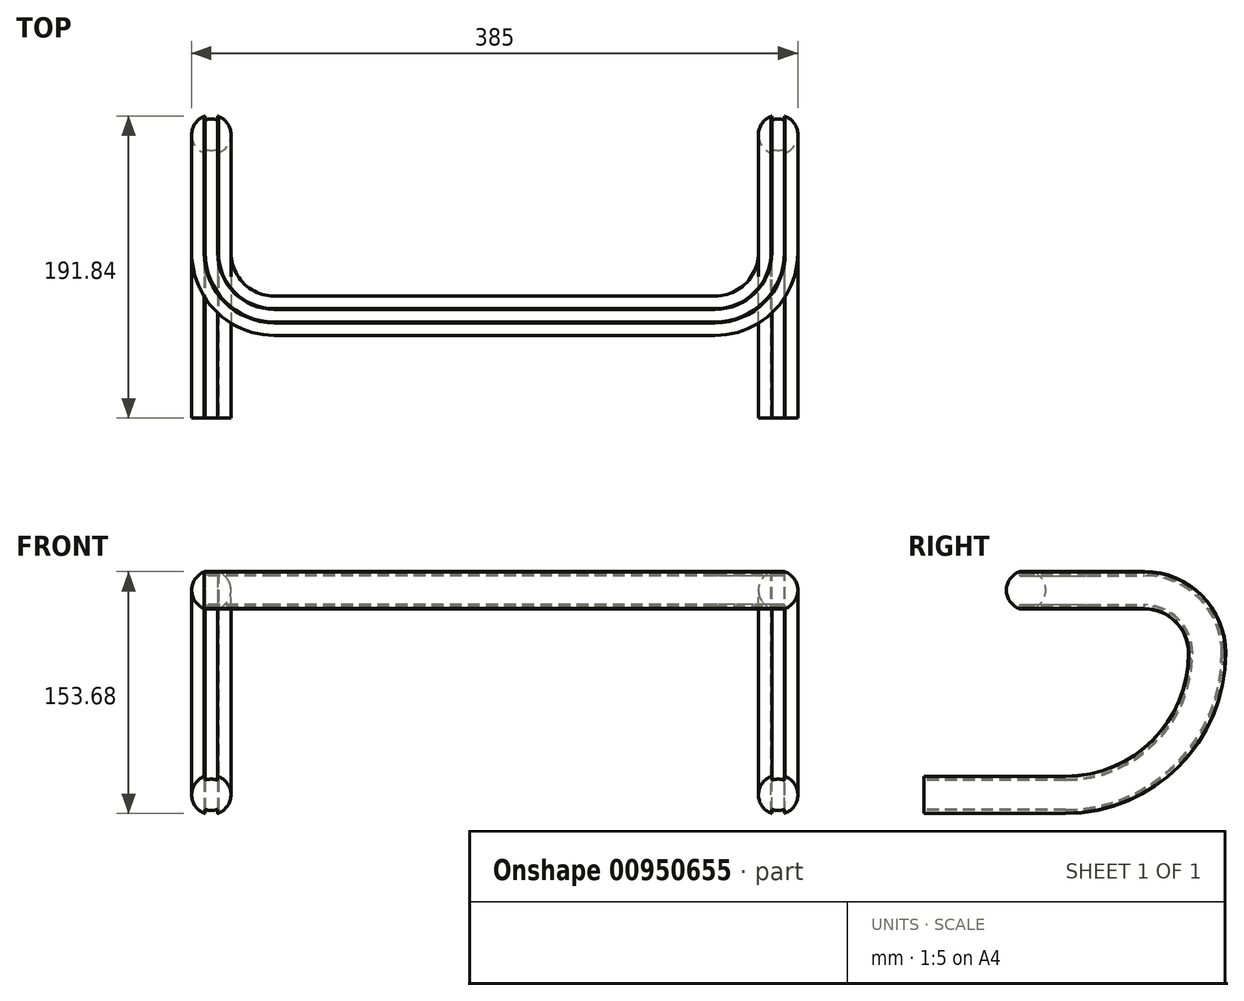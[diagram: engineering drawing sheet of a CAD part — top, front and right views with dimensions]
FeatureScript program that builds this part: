
annotation { "Feature Type Name" : "Feature", "Feature Type Description" : "" }
export const myFeature = defineFeature(function(context is Context, id is Id, definition is map)
    precondition{}
    {
        {
            var Q0;
            Q0=qCreatedBy(makeId("Top.planeOp"),FACE);
            var sketch = newSketch(context, id + "F0", { "sketchPlane" : qUnion([Q0])});
            skLineSegment(sketch, "E0", {"start": v(-140, 0) * mm, "end": v(140, 0) * mm});
            skArc(sketch, "E1", {"start": v(-180, 40) * mm, "mid": v(-168.28, 11.72) * mm, "end": v(-140, 0) * mm});
            skArc(sketch, "E2", {"start": v(140, 0) * mm, "mid": v(168.28, 11.72) * mm, "end": v(180, 40) * mm});
            skSolve(sketch);
        }
        {
            var Q0;
            Q0=qCreatedBy(makeId("Right.planeOp"),FACE);
            var Q1;
            Q1=sQuery(id+"F0.wireOp",VERTEX,"E2.end");
            cPlane(context, id + "F1", {"entities" : qUnion([Q0, Q1]), "cplaneType" : CPlaneType.PLANE_POINT, "offset" : 25 * mm, "width" : 150 * mm, "height" : 150 * mm});
        }
        {
            var Q0;
            Q0=qCreatedBy(id+"F1.planeOp",FACE);
            var sketch = newSketch(context, id + "F2", { "sketchPlane" : qUnion([Q0])});
            skPoint(sketch, "E3.0", {"position": v(40, 0) * mm});
            skLineSegment(sketch, "E4", {"start": v(40, 0) * mm, "end": v(75, 0) * mm});
            skArc(sketch, "E5", {"start": v(115, -40) * mm, "mid": v(103.28, -11.72) * mm, "end": v(75, 0) * mm});
            skArc(sketch, "E6", {"start": v(25, -130) * mm, "mid": v(88.64, -103.64) * mm, "end": v(115, -40) * mm});
            skLineSegment(sketch, "E7", {"start": v(25, -130) * mm, "end": v(-65, -130) * mm});
            skSolve(sketch);
        }
        {
            var Q0;
            Q0=sQuery(id+"F0.wireOp",VERTEX,"E1.start");
            var Q1;
            Q1=qCreatedBy(id+"F1.planeOp",FACE);
            cPlane(context, id + "F3", {"entities" : qUnion([Q0, Q1]), "cplaneType" : CPlaneType.PLANE_POINT, "offset" : 25 * mm, "width" : 150 * mm, "height" : 150 * mm});
        }
        {
            var Q0;
            Q0=qCreatedBy(id+"F3.planeOp",FACE);
            var sketch = newSketch(context, id + "F4", { "sketchPlane" : qUnion([Q0])});
            skLineSegment(sketch, "E8.0", {"start": v(40, 0) * mm, "end": v(75, 0) * mm});
            skArc(sketch, "E8.1", {"start": v(115, -40) * mm, "mid": v(103.28, -11.72) * mm, "end": v(75, 0) * mm});
            skArc(sketch, "E8.2", {"start": v(25, -130) * mm, "mid": v(88.64, -103.64) * mm, "end": v(115, -40) * mm});
            skLineSegment(sketch, "E8.3", {"start": v(25, -130) * mm, "end": v(-65, -130) * mm});
            skSolve(sketch);
        }
        {
            var Q0;
            Q0=qCreatedBy(makeId("Front.planeOp"),FACE);
            var Q1;
            Q1=sQuery(id+"F2.wireOp",VERTEX,"E7.end");
            cPlane(context, id + "F5", {"entities" : qUnion([Q0, Q1]), "cplaneType" : CPlaneType.PLANE_POINT, "offset" : 25 * mm, "width" : 150 * mm, "height" : 150 * mm});
        }
        {
            var Q0;
            Q0=qCreatedBy(id+"F5.planeOp",FACE);
            var sketch = newSketch(context, id + "F6", { "sketchPlane" : qUnion([Q0])});
            skPoint(sketch, "E9.0", {"position": v(180, -130) * mm});
            skArc(sketch, "E10", {"start": v(175.5, -141.66) * mm, "mid": v(175.75, -141.75) * mm, "end": v(176, -141.84) * mm, "construction": true});
            skArc(sketch, "E11", {"start": v(176, -139.17) * mm, "mid": v(180, -140) * mm, "end": v(184, -139.17) * mm, "construction": true});
            skArc(sketch, "E12.trimOffspring", {"start": v(184.5, -118.34) * mm, "mid": v(184.25, -118.25) * mm, "end": v(184, -118.16) * mm, "construction": true});
            skArc(sketch, "E13.trimOffspring", {"start": v(184, -120.83) * mm, "mid": v(180, -120) * mm, "end": v(176, -120.83) * mm, "construction": true});
            skArc(sketch, "E14.trimOffspring", {"start": v(176, -118.16) * mm, "mid": v(175.75, -118.25) * mm, "end": v(175.5, -118.34) * mm, "construction": true});
            skArc(sketch, "E15.trimOffspring", {"start": v(184, -141.84) * mm, "mid": v(184.25, -141.75) * mm, "end": v(184.5, -141.66) * mm, "construction": true});
            skArc(sketch, "E16", {"start": v(175.5, -116.26) * mm, "mid": v(165.54, -130) * mm, "end": v(175.5, -143.74) * mm});
            skArc(sketch, "E17.trimOffspring", {"start": v(184.5, -143.74) * mm, "mid": v(194.46, -130) * mm, "end": v(184.5, -116.26) * mm});
            skLineSegment(sketch, "E18", {"start": v(175.5, -116.26) * mm, "end": v(175.5, -118.34) * mm, "construction": true});
            skLineSegment(sketch, "E19", {"start": v(176, -118.16) * mm, "end": v(176, -120.83) * mm, "construction": true});
            skLineSegment(sketch, "E20", {"start": v(184.5, -116.26) * mm, "end": v(184.5, -118.34) * mm, "construction": true});
            skLineSegment(sketch, "E21", {"start": v(184, -118.16) * mm, "end": v(184, -120.83) * mm, "construction": true});
            skLineSegment(sketch, "E22", {"start": v(176, -141.84) * mm, "end": v(176, -139.17) * mm, "construction": true});
            skLineSegment(sketch, "E23", {"start": v(184, -141.84) * mm, "end": v(184, -139.17) * mm, "construction": true});
            skLineSegment(sketch, "E24", {"start": v(184.5, -143.74) * mm, "end": v(184.5, -141.66) * mm, "construction": true});
            skLineSegment(sketch, "E25", {"start": v(175.5, -116.26) * mm, "end": v(175.5, -118.34) * mm});
            skLineSegment(sketch, "E26", {"start": v(176, -118.16) * mm, "end": v(176, -120.83) * mm});
            skLineSegment(sketch, "E27", {"start": v(184.5, -116.26) * mm, "end": v(184.5, -118.34) * mm});
            skLineSegment(sketch, "E28", {"start": v(184.5, -118.34) * mm, "end": v(184, -118.16) * mm});
            skLineSegment(sketch, "E29", {"start": v(184, -118.16) * mm, "end": v(184, -120.83) * mm});
            skLineSegment(sketch, "E30", {"start": v(175.5, -143.74) * mm, "end": v(175.5, -141.66) * mm});
            skLineSegment(sketch, "E31", {"start": v(175.5, -141.66) * mm, "end": v(176, -141.84) * mm});
            skLineSegment(sketch, "E32", {"start": v(176, -141.84) * mm, "end": v(176, -139.17) * mm});
            skLineSegment(sketch, "E33", {"start": v(184, -139.17) * mm, "end": v(184, -141.84) * mm});
            skLineSegment(sketch, "E34", {"start": v(184, -141.84) * mm, "end": v(184.5, -141.66) * mm});
            skLineSegment(sketch, "E35", {"start": v(184.5, -141.66) * mm, "end": v(184.5, -143.74) * mm});
            skArc(sketch, "E36", {"start": v(176, -139.17) * mm, "mid": v(180, -140) * mm, "end": v(184, -139.17) * mm});
            skArc(sketch, "E37.trimOffspring", {"start": v(184, -120.83) * mm, "mid": v(180, -120) * mm, "end": v(176, -120.83) * mm});
            skCircle(sketch, "E38", {"center": v(180, -130) * mm, "radius": 12.5 * mm});
            skCircle(sketch, "E39", {"center": v(180, -130) * mm, "radius": 10 * mm});
            skLineSegment(sketch, "E40", {"start": v(176, -120.83) * mm, "end": v(176, -139.17) * mm});
            skLineSegment(sketch, "E41", {"start": v(184, -120.83) * mm, "end": v(184, -139.17) * mm});
            skLineSegment(sketch, "E42", {"start": v(175.5, -116.26) * mm, "end": v(175.5, -143.74) * mm});
            skLineSegment(sketch, "E43", {"start": v(184.5, -116.26) * mm, "end": v(184.5, -143.74) * mm});
            skSolve(sketch);
        }
        {
            var Q0;
            {var subQ0=sQuery(id+"F6.wireOp",EDGE,"E42");var subQ1=sQuery(id+"F6.wireOp",EDGE,"E39");var subQ2=makeQuery(id+"F6.imprint","INTERSECT",VERTEX,{"disambiguationData":[OD(0.0)],"derivedFrom":[subQ1,subQ0]});Q0=makeQuery(id+"F6.imprint","IMPRINT",FACE,{"disambiguationData":[TD([[makeQuery(id+"F6.imprint","IMPRINT",EDGE,{"disambiguationData":[TD([[subQ2,-1.0]])],"derivedFrom":subQ1}),1.0]])]});}
            var Q1;
            {var subQ0=sQuery(id+"F6.wireOp",EDGE,"E40");Q1=makeQuery(id+"F6.imprint","IMPRINT",FACE,{"disambiguationData":[TD([[makeQuery(id+"F6.imprint","IMPRINT",EDGE,{"derivedFrom":subQ0}),-1.0]])]});}
            var Q2;
            {var subQ0=sQuery(id+"F6.wireOp",EDGE,"E40");Q2=makeQuery(id+"F6.imprint","IMPRINT",FACE,{"disambiguationData":[TD([[makeQuery(id+"F6.imprint","IMPRINT",EDGE,{"derivedFrom":subQ0}),1.0]])]});}
            var Q3;
            {var subQ0=sQuery(id+"F6.wireOp",EDGE,"E41");Q3=makeQuery(id+"F6.imprint","IMPRINT",FACE,{"disambiguationData":[TD([[makeQuery(id+"F6.imprint","IMPRINT",EDGE,{"derivedFrom":subQ0}),1.0]])]});}
            var Q4;
            {var subQ0=sQuery(id+"F6.wireOp",EDGE,"E43");var subQ1=sQuery(id+"F6.wireOp",EDGE,"E39");var subQ2=makeQuery(id+"F6.imprint","INTERSECT",VERTEX,{"disambiguationData":[OD(0.0)],"derivedFrom":[subQ1,subQ0]});Q4=makeQuery(id+"F6.imprint","IMPRINT",FACE,{"disambiguationData":[TD([[makeQuery(id+"F6.imprint","IMPRINT",EDGE,{"disambiguationData":[TD([[subQ2,1.0]])],"derivedFrom":subQ1}),1.0]])]});}
            var Q5;
            {var subQ0=sQuery(id+"F6.wireOp",EDGE,"E42");var subQ4=sQuery(id+"F6.wireOp",EDGE,"E39");var subQ5=makeQuery(id+"F6.imprint","INTERSECT",VERTEX,{"disambiguationData":[OD(0.0)],"derivedFrom":[subQ4,subQ0]});Q5=makeQuery(id+"F6.imprint","IMPRINT",FACE,{"disambiguationData":[TD([[makeQuery(id+"F6.imprint","IMPRINT",EDGE,{"disambiguationData":[TD([[subQ5,-1.0]])],"derivedFrom":subQ4}),-1.0]])]});}
            var Q6;
            {var subQ0=sQuery(id+"F6.wireOp",EDGE,"E43");var subQ4=sQuery(id+"F6.wireOp",EDGE,"E39");var subQ5=makeQuery(id+"F6.imprint","INTERSECT",VERTEX,{"disambiguationData":[OD(0.0)],"derivedFrom":[subQ4,subQ0]});Q6=makeQuery(id+"F6.imprint","IMPRINT",FACE,{"disambiguationData":[TD([[makeQuery(id+"F6.imprint","IMPRINT",EDGE,{"disambiguationData":[TD([[subQ5,1.0]])],"derivedFrom":subQ4}),-1.0]])]});}
            var Q7;
            {var subQ0=sQuery(id+"F6.wireOp",EDGE,"E17.trimOffspring");Q7=makeQuery(id+"F6.imprint","IMPRINT",FACE,{"disambiguationData":[TD([[makeQuery(id+"F6.imprint","IMPRINT",EDGE,{"derivedFrom":subQ0}),1.0]])]});}
            var Q8;
            {var subQ0=sQuery(id+"F6.wireOp",EDGE,"E16");Q8=makeQuery(id+"F6.imprint","IMPRINT",FACE,{"disambiguationData":[TD([[makeQuery(id+"F6.imprint","IMPRINT",EDGE,{"derivedFrom":subQ0}),1.0]])]});}
            var Q9;
            {var subQ0=sQuery(id+"F6.wireOp",EDGE,"E26");Q9=makeQuery(id+"F6.imprint","IMPRINT",FACE,{"disambiguationData":[TD([[makeQuery(id+"F6.imprint","IMPRINT",EDGE,{"derivedFrom":subQ0}),-1.0]])]});}
            var Q10;
            {var subQ0=sQuery(id+"F6.wireOp",EDGE,"E28");Q10=makeQuery(id+"F6.imprint","IMPRINT",FACE,{"disambiguationData":[TD([[makeQuery(id+"F6.imprint","IMPRINT",EDGE,{"derivedFrom":subQ0}),1.0]])]});}
            var Q11;
            {var subQ0=sQuery(id+"F6.wireOp",EDGE,"E31");Q11=makeQuery(id+"F6.imprint","IMPRINT",FACE,{"disambiguationData":[TD([[makeQuery(id+"F6.imprint","IMPRINT",EDGE,{"derivedFrom":subQ0}),1.0]])]});}
            var Q12;
            {var subQ0=sQuery(id+"F6.wireOp",EDGE,"E33");Q12=makeQuery(id+"F6.imprint","IMPRINT",FACE,{"disambiguationData":[TD([[makeQuery(id+"F6.imprint","IMPRINT",EDGE,{"derivedFrom":subQ0}),1.0]])]});}
            var Q13;
            Q13=sQuery(id+"F2.wireOp",EDGE,"E7");
            var Q14;
            Q14=sQuery(id+"F2.wireOp",EDGE,"E6");
            var Q15;
            Q15 = qConstructionFilter(qBodyType(qCreatedBy(id + "F0" ,EDGE), BodyType.WIRE), ConstructionObject.NO);
            var Q16;
            Q16=sQuery(id+"F2.wireOp",EDGE,"E5");
            var Q17;
            Q17=sQuery(id+"F2.wireOp",EDGE,"E4");
            var Q18;
            Q18=sQuery(id+"F4.wireOp",EDGE,"E8.0");
            var Q19;
            Q19=sQuery(id+"F4.wireOp",EDGE,"E8.1");
            var Q20;
            Q20=sQuery(id+"F4.wireOp",EDGE,"E8.2");
            var Q21;
            Q21=sQuery(id+"F4.wireOp",EDGE,"E8.3");
            sweep(context, id + "F7", {"profiles" : qUnion([Q0, Q1, Q2, Q3, Q4, Q5, Q6, Q7, Q8, Q9, Q10, Q11, Q12]), "path" : qUnion([Q13, Q14, Q15, Q16, Q17, Q18, Q19, Q20, Q21])});
        }
    });
